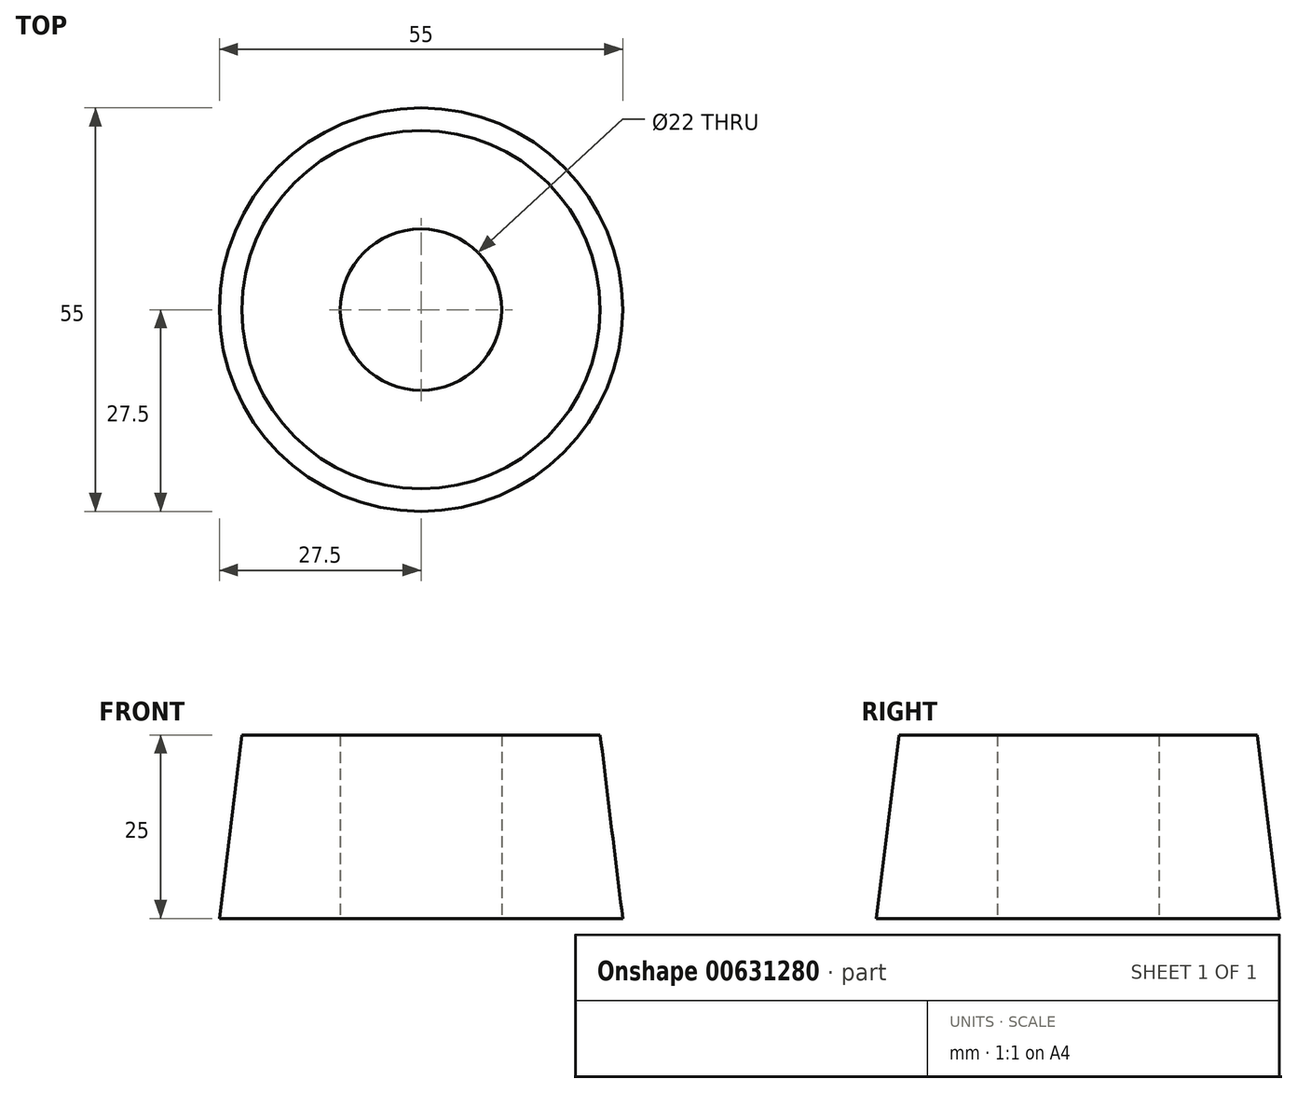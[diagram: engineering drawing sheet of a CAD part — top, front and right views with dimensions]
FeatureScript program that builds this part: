
annotation { "Feature Type Name" : "Feature", "Feature Type Description" : "" }
export const myFeature = defineFeature(function(context is Context, id is Id, definition is map)
    precondition{}
    {
        {
            var Q0;
            Q0=qCreatedBy(makeId("Top.planeOp"),FACE);
            var sketch = newSketch(context, id + "F0", { "sketchPlane" : qUnion([Q0])});
            skCircle(sketch, "E0", {"center": v(0, 0) * mm, "radius": 11 * mm});
            skCircle(sketch, "E1", {"center": v(0, 0) * mm, "radius": 27.5 * mm});
            skSolve(sketch);
        }
        {
            var Q0;
            Q0=makeQuery(id+"F0.imprint","IMPRINT",FACE,{"disambiguationData":[TD([[makeQuery(id+"F0.imprint","IMPRINT",EDGE,{"derivedFrom":sQuery(id+"F0.wireOp",EDGE,"E0")}),-1.0]])]});
            var Q1;
            Q1=makeQuery(id+"F0.imprint","IMPRINT",FACE,{"disambiguationData":[TD([[makeQuery(id+"F0.imprint","IMPRINT",EDGE,{"derivedFrom":sQuery(id+"F0.wireOp",EDGE,"E0")}),1.0]])]});
            extrude(context, id + "F1", {"entities" : qUnion([Q0, Q1]), "depth" : 25 * mm, "offsetDistance" : 25 * mm, "hasDraft" : true, "draftAngle" : 7 * degree, "draftPullDirection" : true});
        }
        {
            var Q0;
            Q0=makeQuery(id+"F0.imprint","IMPRINT",FACE,{"disambiguationData":[TD([[makeQuery(id+"F0.imprint","IMPRINT",EDGE,{"derivedFrom":sQuery(id+"F0.wireOp",EDGE,"E0")}),1.0]])]});
            extrude(context, id + "F2", {"entities" : qUnion([Q0]), "operationType" : NewBodyOperationType.REMOVE, "endBound" : BoundingType.SYMMETRIC, "depth" : 60 * mm, "offsetDistance" : 25 * mm});
        }
    });
